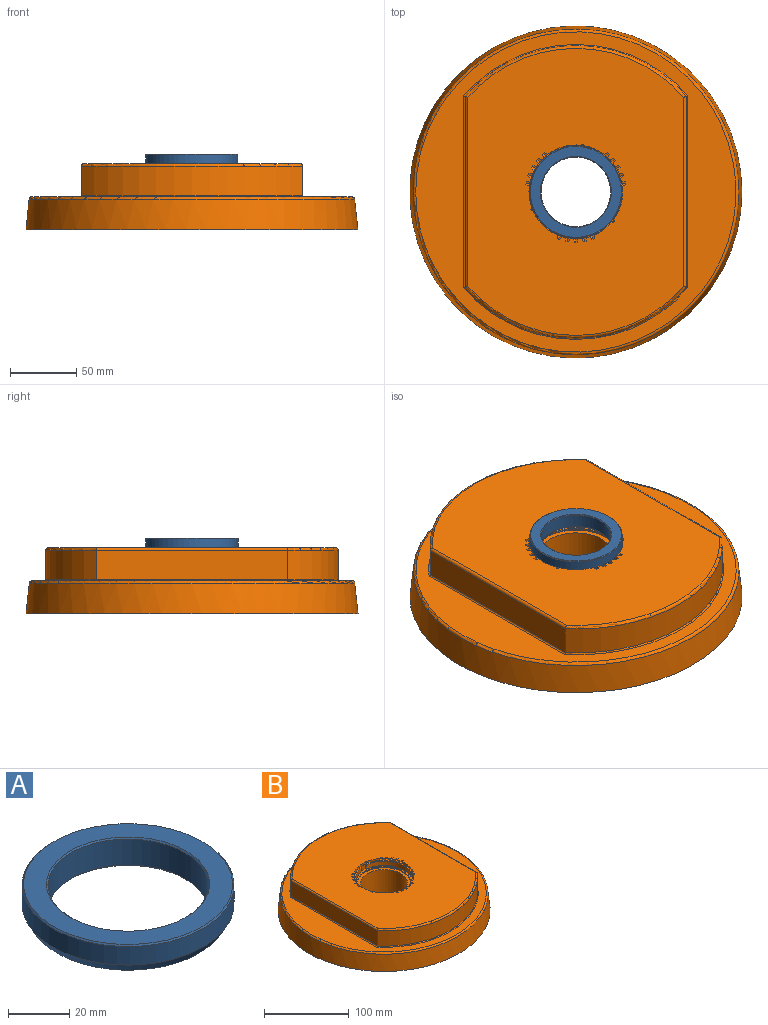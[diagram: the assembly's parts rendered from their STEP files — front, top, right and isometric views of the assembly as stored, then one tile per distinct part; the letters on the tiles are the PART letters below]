
ASSEMBLY  parts=2 mates=1
PART A: 8 faces, bbox 69.4x69.4x11.4 mm
  f0: plane 65.4x65.4mm, normal (0,0,-1), area 1119.7mm2, adj f4,f5
  f1: cylinder r=26.2mm len=52.4mm, axis (0,0,1), area 1712mm2, adj f5,f7
  f2: plane 68.4x68.4mm, normal (0,0,1), area 1434.9mm2, adj f6,f7
  f3: cylinder r=34.7mm len=69.4mm, axis (0,0,1), area 1621.2mm2, adj f4,f6
  f4: cone r=34.7mm half-angle=30deg, axis (0,0,1), area 847mm2, adj f0,f3
  f5: cone r=26.7mm half-angle=45deg, axis (0,0,-1), area 117.5mm2, adj f0,f1
  f6: cone r=34.2mm half-angle=45deg, axis (0,0,-1), area 153.1mm2, adj f2,f3
  f7: cone r=26.2mm half-angle=45deg, axis (0,0,1), area 117.5mm2, adj f1,f2
PART B: 123 faces, bbox 265.3x265.3x50 mm
  f0: cylinder r=33.5mm len=46.81mm, axis (0,0,1), area 388.3mm2, adj f105,f110,f115,f116
  f1: cylinder r=33.5mm len=54.05mm, axis (0,0,1), area 388.3mm2, adj f102,f107,f112,f114
  f2: plane 70.6x70.6mm, normal (0,0,1), area 321.4mm2, adj f101,f102,f103,f104,f105,f106,f107,f108
  f3: cylinder r=33.5mm len=46.81mm, axis (0,0,1), area 388.3mm2, adj f104,f108,f111,f113
  f4: plane 2.2x1.69mm, normal (-0.64,-0.77,0), area 4.4mm2, adj f5,f6,f7,f8,f74
  f5: plane 2.52x1.8mm, normal (-0.89,0.45,0), area 5.1mm2, adj f4,f6,f74,f101
  f6: bspline ~3.23x2.61mm, area 4.1mm2, adj f4,f5,f7,f101
  f7: bspline ~3.11x2.81mm, area 4.1mm2, adj f4,f6,f8,f101
  f8: plane 2.26x1.8mm, normal (0.6,-0.8,0), area 5.1mm2, adj f4,f7,f74,f101
  f9: plane 2.2x1.69mm, normal (-0.77,-0.64,0), area 4.4mm2, adj f10,f11,f12,f13,f74
  f10: plane 2.26x1.8mm, normal (-0.8,0.6,0), area 5.1mm2, adj f9,f11,f74,f101
  f11: bspline ~3.11x2.81mm, area 4.1mm2, adj f9,f10,f12,f101
  f12: bspline ~3.23x2.61mm, area 4.1mm2, adj f9,f11,f13,f101
  f13: plane 2.52x1.8mm, normal (0.45,-0.89,0), area 5.1mm2, adj f9,f12,f74,f101
  f14: plane 2.2x2.17mm, normal (-0.98,-0.17,0), area 4.4mm2, adj f15,f16,f17,f18,f74
  f15: plane 2.59x1.8mm, normal (-0.4,0.92,0), area 5.1mm2, adj f14,f16,f74,f101
  f16: bspline ~8.07x4.34mm, area 4.1mm2, adj f14,f15,f17,f101
  f17: bspline ~8.4x2.95mm, area 4.1mm2, adj f14,f16,f18,f101
  f18: plane 2.82x1.8mm, normal (-0.06,-1,0), area 5.1mm2, adj f14,f17,f74,f101
  f19: plane 2.2x2.07mm, normal (-0.94,-0.34,0), area 4.4mm2, adj f20,f21,f22,f23,f74
  f20: plane 2.36x1.8mm, normal (-0.55,0.84,0), area 5.1mm2, adj f19,f21,f74,f101
  f21: bspline ~2.95x2.58mm, area 4.1mm2, adj f19,f20,f22,f101
  f22: bspline ~3.18x1.97mm, area 4.1mm2, adj f19,f21,f23,f101
  f23: plane 2.8x1.8mm, normal (0.12,-0.99,0), area 5.1mm2, adj f19,f22,f74,f101
  f24: plane 2.2x1.91mm, normal (-0.87,-0.5,0), area 4.4mm2, adj f25,f26,f27,f28,f74
  f25: plane 2.05x1.94mm, normal (-0.69,0.73,0), area 5.1mm2, adj f24,f26,f74,f101
  f26: bspline ~7.48x6.6mm, area 4.1mm2, adj f24,f25,f27,f101
  f27: bspline ~8.43x4.95mm, area 4.1mm2, adj f24,f26,f28,f101
  f28: plane 2.7x1.8mm, normal (0.29,-0.96,0), area 5.1mm2, adj f24,f27,f74,f101
  f29: plane 2.2x2.17mm, normal (0.98,-0.17,0), area 4.4mm2, adj f30,f31,f32,f33,f74
  f30: plane 2.82x1.8mm, normal (0.06,-1,0), area 5.1mm2, adj f29,f31,f74,f101
  f31: bspline ~8.4x2.95mm, area 4.1mm2, adj f29,f30,f32,f101
  f32: bspline ~8.07x4.34mm, area 4.1mm2, adj f29,f31,f33,f101
  f33: plane 2.59x1.8mm, normal (0.4,0.92,0), area 5.1mm2, adj f29,f32,f74,f101
  f34: plane 2.2x2.07mm, normal (0.94,-0.34,0), area 4.4mm2, adj f35,f36,f37,f38,f74
  f35: plane 2.8x1.8mm, normal (-0.12,-0.99,0), area 5.1mm2, adj f34,f36,f74,f101
  f36: bspline ~3.18x1.97mm, area 4.1mm2, adj f34,f35,f37,f101
  f37: bspline ~2.95x2.58mm, area 4.1mm2, adj f34,f36,f38,f101
  f38: plane 2.36x1.8mm, normal (0.55,0.84,0), area 5.1mm2, adj f34,f37,f74,f101
  f39: plane 2.2x1.69mm, normal (0.64,-0.77,0), area 4.4mm2, adj f40,f41,f42,f43,f74
  f40: plane 2.26x1.8mm, normal (-0.6,-0.8,0), area 5.1mm2, adj f39,f41,f74,f101
  f41: bspline ~3.11x2.81mm, area 4.1mm2, adj f39,f40,f42,f101
  f42: bspline ~3.23x2.61mm, area 4.1mm2, adj f39,f41,f43,f101
  f43: plane 2.52x1.8mm, normal (0.89,0.45,0), area 5.1mm2, adj f39,f42,f74,f101
  f44: plane 2.2x1.69mm, normal (0.77,-0.64,0), area 4.4mm2, adj f45,f46,f47,f48,f74
  f45: plane 2.52x1.8mm, normal (-0.45,-0.89,0), area 5.1mm2, adj f44,f46,f74,f101
  f46: bspline ~3.23x2.61mm, area 4.1mm2, adj f44,f45,f47,f101
  f47: bspline ~3.11x2.81mm, area 4.1mm2, adj f44,f46,f48,f101
  f48: plane 2.26x1.8mm, normal (0.8,0.6,0), area 5.1mm2, adj f44,f47,f74,f101
  f49: plane 2.2x1.91mm, normal (0.87,-0.5,0), area 4.4mm2, adj f50,f51,f52,f53,f74
  f50: plane 2.7x1.8mm, normal (-0.29,-0.96,0), area 5.1mm2, adj f49,f51,f74,f101
  f51: bspline ~8.43x4.95mm, area 4.1mm2, adj f49,f50,f52,f101
  f52: bspline ~7.48x6.6mm, area 4.1mm2, adj f49,f51,f53,f101
  f53: plane 2.05x1.94mm, normal (0.69,0.73,0), area 5.1mm2, adj f49,f52,f74,f101
  f54: plane 2.2x2.07mm, normal (-0.34,0.94,0), area 4.4mm2, adj f55,f56,f57,f58,f74
  f55: plane 2.36x1.8mm, normal (0.84,0.55,0), area 5.1mm2, adj f54,f56,f74,f101
  f56: bspline ~2.95x2.58mm, area 4.1mm2, adj f54,f55,f57,f101
  f57: bspline ~3.18x1.97mm, area 4.1mm2, adj f54,f56,f58,f101
  f58: plane 2.8x1.8mm, normal (-0.99,-0.12,0), area 5.1mm2, adj f54,f57,f74,f101
  f59: plane 2.2x2.17mm, normal (-0.17,0.98,0), area 4.4mm2, adj f60,f61,f62,f63,f74
  f60: plane 2.59x1.8mm, normal (0.92,0.4,0), area 5.1mm2, adj f59,f61,f74,f101
  f61: bspline ~8.07x4.34mm, area 4.1mm2, adj f59,f60,f62,f101
  f62: bspline ~8.4x2.95mm, area 4.1mm2, adj f59,f61,f63,f101
  f63: plane 2.82x1.8mm, normal (-1,0.06,0), area 5.1mm2, adj f59,f62,f74,f101
  f64: plane 2.2x2.07mm, normal (0.34,0.94,0), area 4.4mm2, adj f65,f66,f67,f68,f74
  f65: plane 2.8x1.8mm, normal (0.99,-0.12,0), area 5.1mm2, adj f64,f66,f74,f101
  f66: bspline ~3.18x1.97mm, area 4.1mm2, adj f64,f65,f67,f101
  f67: bspline ~2.95x2.58mm, area 4.1mm2, adj f64,f66,f68,f101
  f68: plane 2.36x1.8mm, normal (-0.84,0.55,0), area 5.1mm2, adj f64,f67,f74,f101
  f69: plane 2.2x2.17mm, normal (0.17,0.98,0), area 4.4mm2, adj f70,f71,f72,f73,f74
  f70: plane 2.82x1.8mm, normal (1,0.06,0), area 5.1mm2, adj f69,f71,f74,f101
  f71: bspline ~8.4x2.95mm, area 4.1mm2, adj f69,f70,f72,f101
  f72: bspline ~8.07x4.34mm, area 4.1mm2, adj f69,f71,f73,f101
  f73: plane 2.59x1.8mm, normal (-0.92,0.4,0), area 5.1mm2, adj f69,f72,f74,f101
  f74: plane 216x162.46mm, normal (0,0,1), area 27387mm2, adj f4,f5,f8,f9,f10,f13,f14,f15
  f75: cylinder r=110mm len=166.46mm, axis (0,0,1), area 4153.6mm2, adj f84,f85,f86,f91
  f76: cone r=125mm half-angle=6.1deg, axis (0,0,-1), area 18153.3mm2, adj f77,f90
  f77: plane 250x250mm, normal (0,0,-1), area 46711.6mm2, adj f76,f78
  f78: cylinder r=27.5mm len=55mm, axis (0,0,1), area 6812.2mm2, adj f77,f79
  f79: plane 62.4x62.4mm, normal (0,0,1), area 682.3mm2, adj f78,f95
  f80: cylinder r=31.5mm len=63mm, axis (0,0,1), area 197.9mm2, adj f81,f95
  f81: plane 68.2x66.6mm, normal (0,0,1), area 400.6mm2, adj f80,f102,f103,f104,f105,f106,f107,f108
  f82: cylinder r=110mm len=166.46mm, axis (0,0,1), area 4153.6mm2, adj f84,f85,f89,f94
  f83: plane 241.05x241.05mm, normal (0,0,1), area 12228.3mm2, adj f90,f91,f92,f93,f94
  f84: plane 143.84x22mm, normal (-1,0,0), area 3164.5mm2, adj f75,f82,f87,f92
  f85: plane 143.84x22mm, normal (1,0,0), area 3164.5mm2, adj f75,f82,f88,f93
  f86: torus R=108mm, axis (0,0,1), area 587.5mm2, adj f74,f75,f87,f88
  f87: cylinder r=2mm len=143.84mm, axis (0,-1,0), area 450.2mm2, adj f74,f84,f86,f89
  f88: cylinder r=2mm len=143.84mm, axis (0,1,0), area 450.2mm2, adj f74,f85,f86,f89
  f89: torus R=108mm, axis (0,0,1), area 587.5mm2, adj f74,f82,f87,f88
  f90: torus R=120.53mm, axis (0,0,-1), area 2240mm2, adj f76,f83
  f91: torus R=111mm, axis (0,0,-1), area 298mm2, adj f75,f83,f92,f93
  f92: cylinder r=1mm len=144.58mm, axis (0,-1,0), area 226.4mm2, adj f83,f84,f91,f94
  f93: cylinder r=1mm len=144.58mm, axis (0,1,0), area 226.4mm2, adj f83,f85,f91,f94
  f94: torus R=111mm, axis (0,0,-1), area 298mm2, adj f82,f83,f92,f93
  f95: torus R=31.2mm, axis (0,0,-1), area 92.9mm2, adj f79,f80
  f96: plane 2.74x1.8mm, normal (-0.97,0.23,0), area 5.1mm2, adj f74,f97,f100,f101
  f97: bspline ~8x3mm, area 4.1mm2, adj f96,f98,f100,f101
  f98: bspline ~8x3mm, area 4.1mm2, adj f97,f99,f100,f101
  f99: plane 2.74x1.8mm, normal (0.97,0.23,0), area 5.1mm2, adj f74,f98,f100,f101
  f100: plane 2.2x2.2mm, normal (0,1,0), area 4.4mm2, adj f74,f96,f97,f98,f99
  f101: cylinder r=35.3mm len=70.6mm, axis (0,0,1), area 485.4mm2, adj f2,f5,f6,f7,f8,f10,f11,f12
  f102: plane 6.6x1.53mm, normal (0.39,0.92,0), area 9.5mm2, adj f1,f2,f81,f103,f112,f114
  f103: cylinder r=34.9mm len=6.58mm, axis (0,0,-1), area 45.5mm2, adj f2,f81,f102,f104
  f104: plane 6.6x1.33mm, normal (-0.6,-0.8,0), area 9.5mm2, adj f2,f3,f81,f103,f111,f113
  f105: plane 6.6x1.33mm, normal (0.6,-0.8,0), area 9.5mm2, adj f0,f2,f81,f106,f115,f116
  f106: cylinder r=34.9mm len=6.58mm, axis (0,0,-1), area 45.5mm2, adj f2,f81,f105,f107
  f107: plane 6.6x1.53mm, normal (-0.39,0.92,0), area 9.5mm2, adj f1,f2,f81,f106,f112,f114
  f108: plane 6.6x1.65mm, normal (-0.99,-0.13,0), area 9.5mm2, adj f2,f3,f81,f109,f111,f113
  f109: cylinder r=34.9mm len=6.9mm, axis (0,0,-1), area 45.5mm2, adj f2,f81,f108,f110
  f110: plane 6.6x1.65mm, normal (0.99,-0.13,0), area 9.5mm2, adj f0,f2,f81,f109,f115,f116
  f111: torus R=33.3mm, axis (0,0,-1), area 19.7mm2, adj f3,f81,f104,f108
  f112: torus R=33.3mm, axis (0,0,-1), area 19.7mm2, adj f1,f81,f102,f107
  f113: torus R=33.7mm, axis (0,0,1), area 19.8mm2, adj f2,f3,f104,f108
  f114: torus R=33.7mm, axis (0,0,1), area 19.8mm2, adj f1,f2,f102,f107
  f115: torus R=33.7mm, axis (0,0,1), area 19.8mm2, adj f0,f2,f105,f110
  f116: torus R=33.3mm, axis (0,0,-1), area 19.7mm2, adj f0,f81,f105,f110
  f117: cylinder r=1mm len=1.93mm, axis (0,0,1), area 1.6mm2, adj f74,f101,f118
  f118: plane 1.93x1.39mm, normal (0,0,1), area 1.6mm2, adj f101,f117
  f119: cylinder r=1mm len=1.8mm, axis (0,0,1), area 1.6mm2, adj f74,f101,f120
  f120: plane 1.8x1.63mm, normal (0,0,1), area 1.6mm2, adj f101,f119
  f121: cylinder r=1mm len=1.99mm, axis (0,0,1), area 1.6mm2, adj f74,f101,f122
  f122: plane 1.99x1.16mm, normal (0,0,1), area 1.6mm2, adj f101,f121
PLACE A t=(53.13,73.44,117.52)mm
PLACE B t=(53.13,73.44,71.72)mm
MATE fastened A.f1 <-> B.f0  axis (0,0,-1) through (53.13,73.44,117.52)mm
